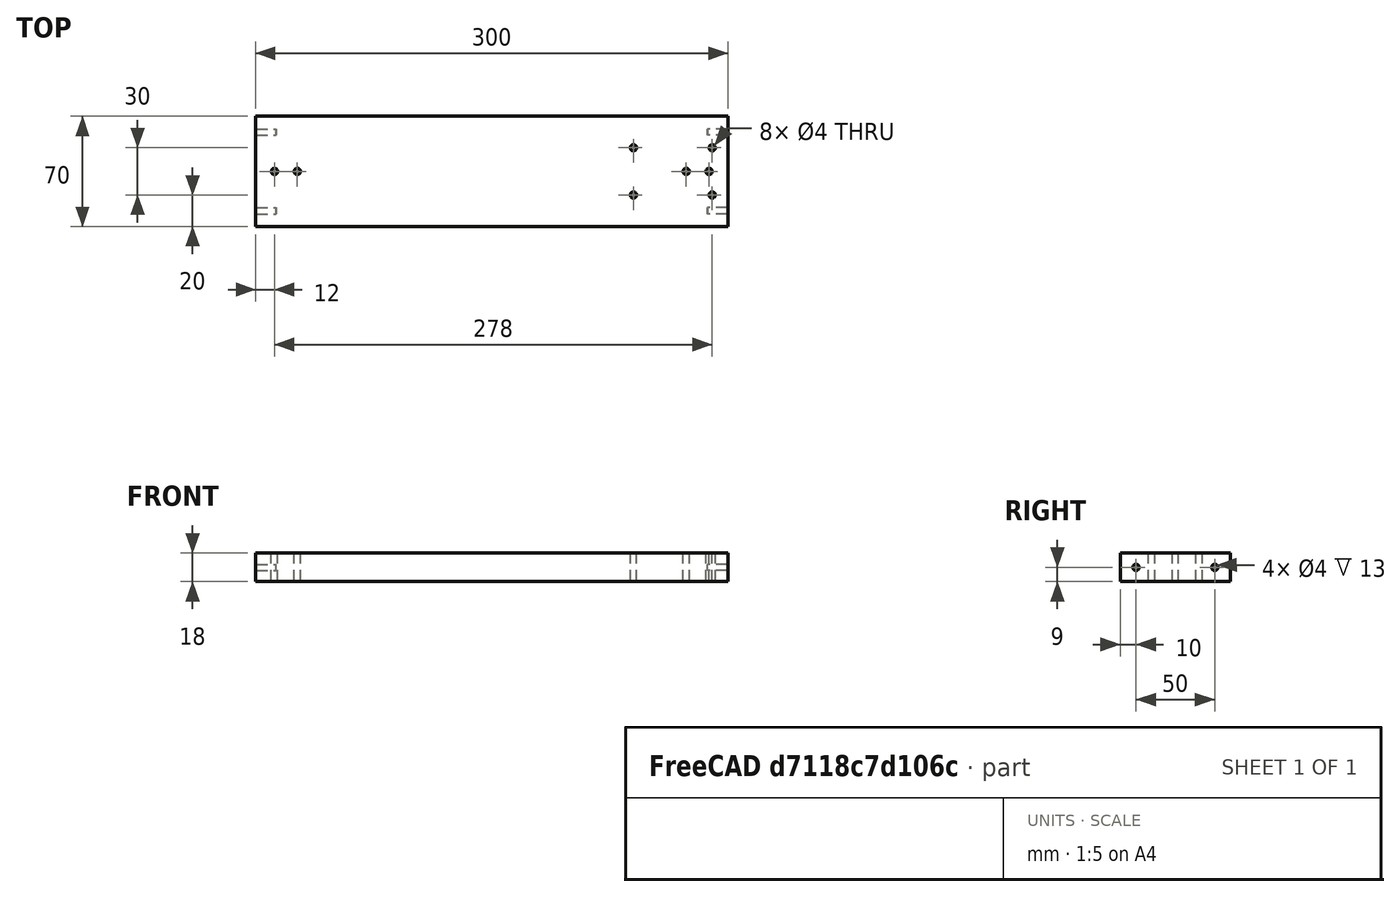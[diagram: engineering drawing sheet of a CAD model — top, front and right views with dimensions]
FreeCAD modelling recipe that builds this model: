
FCSTD DOCUMENT  (FreeCAD 0.17R13541 (Git))
Label: Base-LateralDerecha
License: All rights reserved
LicenseURL: http://en.wikipedia.org/wiki/All_rights_reserved
objects: Part::Cylinder×7, Part::MultiFuse×4, Part::Cut×3, Part::Box×1, Part::FeaturePython×1, Part::Mirroring×1
note: 17 computed .brp shape members not serialized (recipe doc carries the construction recipe); baked Part::Feature solids carry a one-line shape summary decoded from their .brp

FEATURE [Part::Box] Box  label="Cubo"
  AttacherType = Attacher::AttachEngine3D
  Height = 18
  Length = 300
  Width = 70
FEATURE [Part::Cylinder] Cylinder  label="Cilindro"
  Angle = 360
  AttacherType = Attacher::AttachEngine3D
  Height = 25
  Placement = pos=(12,35,0) rot=(0,0,1;0rad)
  Radius = 2
FEATURE [Part::Cylinder] Cylinder001  label="Cilindro001"
  Angle = 360
  AttacherType = Attacher::AttachEngine3D
  Height = 25
  Placement = pos=(26.5,35,0) rot=(0,0,1;0rad)
  Radius = 2
FEATURE [Part::Cylinder] Cylinder002  label="Cilindro002"
  Angle = 360
  AttacherType = Attacher::AttachEngine3D
  Height = 25
  Radius = 2
FEATURE [Part::FeaturePython] Array  # Draft array (typed FeaturePython)
  Angle = 360
  ArrayType = 0
  Axis = (0,0,1)
  Base = -> Cylinder002
  Center = (0,0,0)
  Fuse = false
  IntervalAxis = (0,0,0)
  IntervalX = (50,0,0)
  IntervalY = (0,30,0)
  IntervalZ = (0,0,0)
  NumberPolar = 1
  NumberX = 2
  NumberY = 2
  NumberZ = 1
  Placement = pos=(240,20,0) rot=(0,0,1;0rad)
FEATURE [Part::MultiFuse] Fusion
  Refine = true
  Shapes = -> [Cylinder,Cylinder001]
FEATURE [Part::Cylinder] Cylinder003  label="Cilindro003"
  Angle = 360
  AttacherType = Attacher::AttachEngine3D
  Height = 25
  Placement = pos=(26.5,35,0) rot=(0,0,1;0rad)
  Radius = 2
FEATURE [Part::Cylinder] Cylinder004  label="Cilindro004"
  Angle = 360
  AttacherType = Attacher::AttachEngine3D
  Height = 25
  Placement = pos=(12,35,0) rot=(0,0,1;0rad)
  Radius = 2
FEATURE [Part::MultiFuse] Fusion001
  Placement = pos=(261.5,0,0) rot=(0,0,1;0rad)
  Refine = true
  Shapes = -> [Cylinder004,Cylinder003]
FEATURE [Part::MultiFuse] Fusion002
  Refine = true
  Shapes = -> [Fusion,Fusion001,Array]
FEATURE [Part::Cut] Cut
  Base = -> Box
  Refine = true
  Tool = -> Fusion002
FEATURE [Part::Cylinder] Cylinder005  label="Cilindro005"
  Angle = 360
  AttacherType = Attacher::AttachEngine3D
  Height = 13
  Placement = pos=(0,10,9) rot=(0,1,0;1.5708rad)
  Radius = 2
FEATURE [Part::Cylinder] Cylinder006  label="Cilindro006"
  Angle = 360
  AttacherType = Attacher::AttachEngine3D
  Height = 13
  Placement = pos=(0,60,9) rot=(0,1,0;1.5708rad)
  Radius = 2
FEATURE [Part::MultiFuse] Fusion003
  Refine = true
  Shapes = -> [Cylinder006,Cylinder005]
FEATURE [Part::Mirroring] mirror  label="Mirror of Fusion003"
  Base = (300,0,18)
  Normal = (0.91,0,0)
  Placement = pos=(-300,0,0) rot=(0,0,1;0rad)
  Source = -> Fusion003
FEATURE [Part::Cut] Cut001
  Base = -> Cut
  Refine = true
  Tool = -> mirror
FEATURE [Part::Cut] Cut002
  Base = -> Cut001
  Refine = true
  Tool = -> Fusion003
